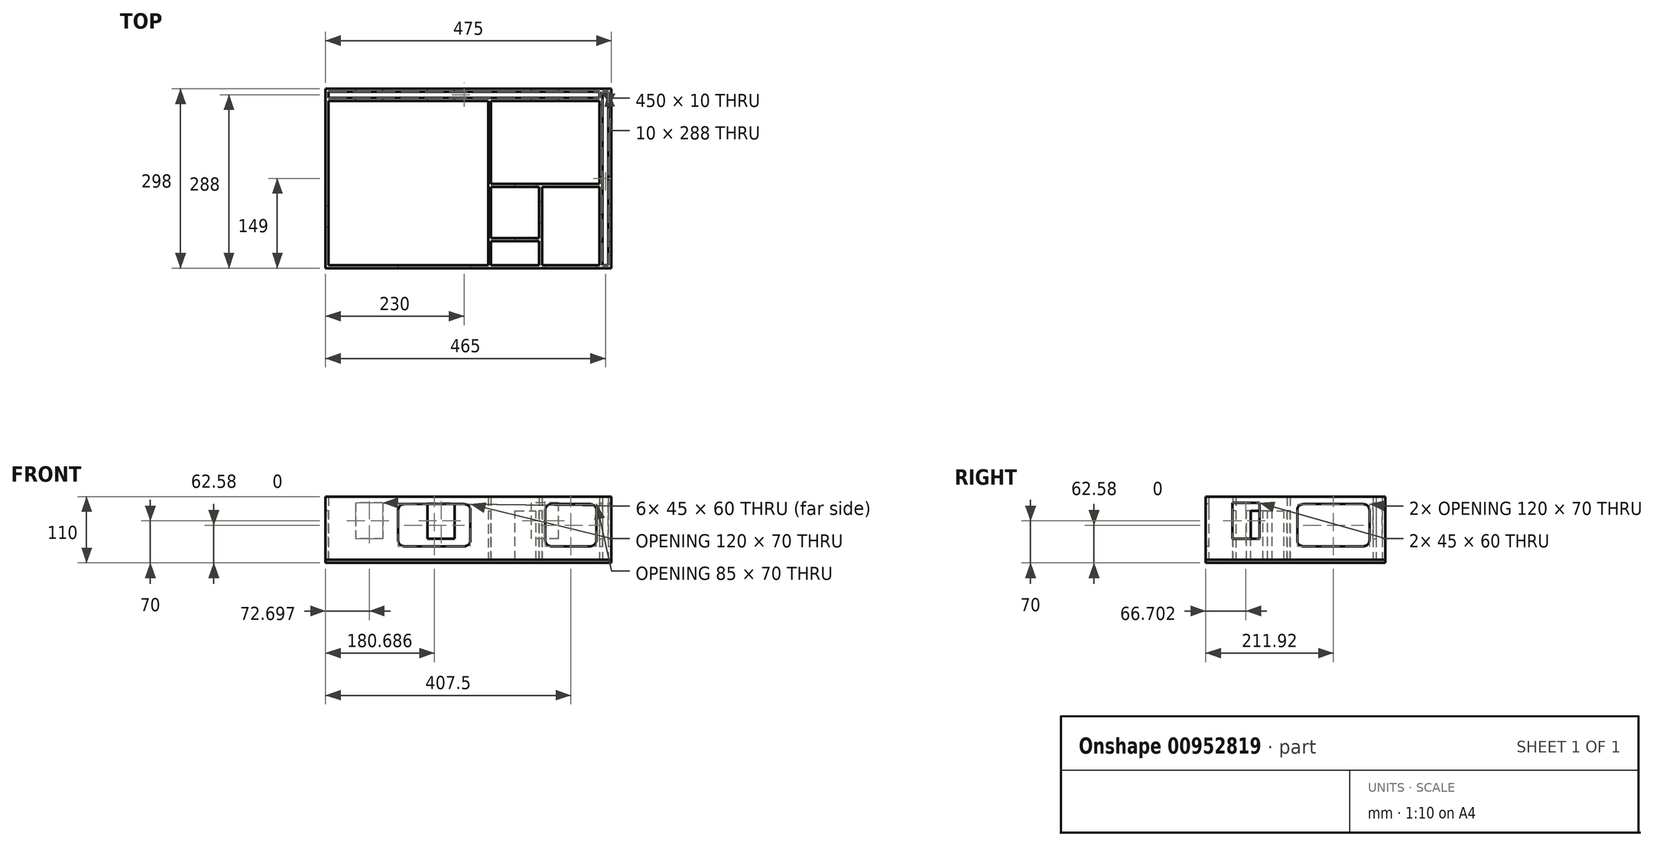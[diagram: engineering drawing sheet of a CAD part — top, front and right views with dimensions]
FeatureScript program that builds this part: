
annotation { "Feature Type Name" : "Feature", "Feature Type Description" : "" }
export const myFeature = defineFeature(function(context is Context, id is Id, definition is map)
    precondition{}
    {
        {
            var Q0;
            Q0=qCreatedBy(makeId("Top.planeOp"),FACE);
            var sketch = newSketch(context, id + "F0", { "sketchPlane" : qUnion([Q0])});
            skLineSegment(sketch, "E0.bottom", {"start": v(237.5, -149) * mm, "end": v(-237.5, -149) * mm});
            skLineSegment(sketch, "E0.top", {"start": v(237.5, 149) * mm, "end": v(-237.5, 149) * mm});
            skLineSegment(sketch, "E0.left", {"start": v(237.5, -149) * mm, "end": v(237.5, 149) * mm});
            skLineSegment(sketch, "E0.right", {"start": v(-237.5, -149) * mm, "end": v(-237.5, 149) * mm});
            skPoint(sketch, "E0.middle", {"position": v(0, 0) * mm});
            skSolve(sketch);
        }
        {
            var Q0;
            Q0 = qSketchRegion(id + "F0", true);
            extrude(context, id + "F1", {"entities" : qUnion([Q0]), "oppositeDirection" : true, "depth" : 5 * mm, "offsetDistance" : 25 * mm});
        }
        {
            var Q0;
            Q0=makeQuery(id+"F1.opExtrude","CAP_FACE",FACE,{"disambiguationData":[OSD([sQuery(id+"F0.wireOp",EDGE,"E0.bottom"),sQuery(id+"F0.wireOp",EDGE,"E0.top"),sQuery(id+"F0.wireOp",EDGE,"E0.left"),sQuery(id+"F0.wireOp",EDGE,"E0.right")])],"isStart":true});
            var sketch = newSketch(context, id + "F2", { "sketchPlane" : qUnion([Q0])});
            skLineSegment(sketch, "E1.0.0", {"start": v(237.5, -149) * mm, "end": v(237.5, 149) * mm});
            skLineSegment(sketch, "E1.0.1", {"start": v(237.5, 149) * mm, "end": v(-237.5, 149) * mm});
            skLineSegment(sketch, "E1.0.2", {"start": v(-237.5, 149) * mm, "end": v(-237.5, -149) * mm});
            skLineSegment(sketch, "E1.0.3", {"start": v(-237.5, -149) * mm, "end": v(237.5, -149) * mm});
            skLineSegment(sketch, "E2.0", {"start": v(232.5, -144) * mm, "end": v(232.5, 144) * mm});
            skLineSegment(sketch, "E2.1", {"start": v(-232.5, -144) * mm, "end": v(232.5, -144) * mm});
            skLineSegment(sketch, "E2.2", {"start": v(-232.5, 144) * mm, "end": v(-232.5, -144) * mm});
            skLineSegment(sketch, "E2.3", {"start": v(232.5, 144) * mm, "end": v(-232.5, 144) * mm});
            skLineSegment(sketch, "E3", {"start": v(-232.5, 134) * mm, "end": v(217.5, 134) * mm});
            skLineSegment(sketch, "E4", {"start": v(-232.5, 129) * mm, "end": v(217.5, 129) * mm});
            skLineSegment(sketch, "E5", {"start": v(32.5, 129) * mm, "end": v(32.5, -144) * mm});
            skLineSegment(sketch, "E6", {"start": v(37.5, -144) * mm, "end": v(37.5, 129) * mm});
            skLineSegment(sketch, "E7", {"start": v(222.5, 144) * mm, "end": v(222.5, -144) * mm});
            skLineSegment(sketch, "E8", {"start": v(217.5, 144) * mm, "end": v(217.5, -144) * mm});
            skLineSegment(sketch, "E9", {"start": v(117.5, -14) * mm, "end": v(117.5, -144) * mm});
            skLineSegment(sketch, "E10", {"start": v(122.5, -14) * mm, "end": v(122.5, -144) * mm});
            skLineSegment(sketch, "E11", {"start": v(37.5, -9) * mm, "end": v(217.5, -9) * mm});
            skLineSegment(sketch, "E12", {"start": v(37.5, -14) * mm, "end": v(217.5, -14) * mm});
            skLineSegment(sketch, "E13", {"start": v(117.5, -99) * mm, "end": v(37.5, -99) * mm});
            skLineSegment(sketch, "E14", {"start": v(117.5, -104) * mm, "end": v(37.5, -104) * mm});
            skLineSegment(sketch, "E15", {"start": v(73.5, -104) * mm, "end": v(73.5, -144) * mm, "construction": true});
            skSolve(sketch);
        }
        {
            var Q0;
            Q0=makeQuery(id+"F2.imprint","IMPRINT",FACE,{"disambiguationData":[TD([[makeQuery(id+"F2.imprint","IMPRINT",EDGE,{"derivedFrom":sQuery(id+"F2.wireOp",EDGE,"E1.0.0")}),1.0]])]});
            var Q1;
            {var subQ4=sQuery(id+"F2.wireOp",EDGE,"afQwtqYh-coUw-1QRY-l5fW-YoJflLdhl2Ut");Q1=makeQuery(id+"F2.imprint","IMPRINT",FACE,{"disambiguationData":[TD([[makeQuery(id+"F2.imprint","IMPRINT",EDGE,{"derivedFrom":subQ4}),1.0]])]});}
            var Q2;
            {var subQ5=sQuery(id+"F2.wireOp",EDGE,"E3");Q2=makeQuery(id+"F2.imprint","IMPRINT",FACE,{"disambiguationData":[TD([[makeQuery(id+"F2.imprint","IMPRINT",EDGE,{"derivedFrom":subQ5}),-1.0]])]});}
            var Q3;
            {var subQ0=sQuery(id+"F2.wireOp",EDGE,"E5");Q3=makeQuery(id+"F2.imprint","IMPRINT",FACE,{"disambiguationData":[TD([[makeQuery(id+"F2.imprint","IMPRINT",EDGE,{"derivedFrom":subQ0}),1.0]])]});}
            var Q4;
            {var subQ0=sQuery(id+"F2.wireOp",EDGE,"E7");Q4=makeQuery(id+"F2.imprint","IMPRINT",FACE,{"disambiguationData":[TD([[makeQuery(id+"F2.imprint","IMPRINT",EDGE,{"derivedFrom":subQ0}),-1.0]])]});}
            var Q5;
            {var subQ0=sQuery(id+"F2.wireOp",EDGE,"E9");Q5=makeQuery(id+"F2.imprint","IMPRINT",FACE,{"disambiguationData":[TD([[makeQuery(id+"F2.imprint","IMPRINT",EDGE,{"derivedFrom":subQ0}),1.0]])]});}
            var Q6;
            {var subQ0=sQuery(id+"F2.wireOp",EDGE,"E11");Q6=makeQuery(id+"F2.imprint","IMPRINT",FACE,{"disambiguationData":[TD([[makeQuery(id+"F2.imprint","IMPRINT",EDGE,{"derivedFrom":subQ0}),-1.0]])]});}
            var Q7;
            {var subQ0=sQuery(id+"F2.wireOp",EDGE,"E13");Q7=makeQuery(id+"F2.imprint","IMPRINT",FACE,{"disambiguationData":[TD([[makeQuery(id+"F2.imprint","IMPRINT",EDGE,{"derivedFrom":subQ0}),1.0]])]});}
            extrude(context, id + "F3", {"entities" : qUnion([Q0, Q1, Q2, Q3, Q4, Q5, Q6, Q7]), "depth" : 105 * mm, "offsetDistance" : 25 * mm});
        }
        {
            var Q0;
            Q0=makeQuery(id+"F3.boolean.opBoolean","MERGE",FACE,{"derivedFrom":[makeQuery(id+"F1.opExtrude","SWEPT_FACE",FACE,{"disambiguationData":[OSD([sQuery(id+"F0.wireOp",EDGE,"E0.top")])]}),makeQuery(id+"F3.opExtrude","SWEPT_FACE",FACE,{"disambiguationData":[OSD([sQuery(id+"F2.wireOp",EDGE,"E1.0.1")])]})]});
            var sketch = newSketch(context, id + "F4", { "sketchPlane" : qUnion([Q0])});
            skLineSegment(sketch, "E16.bottom", {"start": v(142.3, 95) * mm, "end": v(187.3, 95) * mm});
            skLineSegment(sketch, "E16.top", {"start": v(142.3, 35) * mm, "end": v(187.3, 35) * mm});
            skLineSegment(sketch, "E16.left", {"start": v(142.3, 95) * mm, "end": v(142.3, 35) * mm});
            skLineSegment(sketch, "E16.right", {"start": v(187.3, 95) * mm, "end": v(187.3, 35) * mm});
            skLineSegment(sketch, "E17.bottom", {"start": v(-104.37, 95) * mm, "end": v(-149.37, 95) * mm});
            skLineSegment(sketch, "E17.top", {"start": v(-104.37, 35) * mm, "end": v(-149.37, 35) * mm});
            skLineSegment(sketch, "E17.left", {"start": v(-104.37, 95) * mm, "end": v(-104.37, 35) * mm});
            skLineSegment(sketch, "E17.right", {"start": v(-149.37, 95) * mm, "end": v(-149.37, 35) * mm});
            skLineSegment(sketch, "E18.bottom", {"start": v(68.09, 95) * mm, "end": v(23.09, 95) * mm});
            skLineSegment(sketch, "E18.top", {"start": v(68.09, 35) * mm, "end": v(23.09, 35) * mm});
            skLineSegment(sketch, "E18.left", {"start": v(68.09, 95) * mm, "end": v(68.09, 35) * mm});
            skLineSegment(sketch, "E18.right", {"start": v(23.09, 95) * mm, "end": v(23.09, 35) * mm});
            skSolve(sketch);
        }
        {
            var Q0;
            Q0=makeQuery(id+"F4.imprint","IMPRINT",FACE,{"disambiguationData":[TD([[makeQuery(id+"F4.imprint","IMPRINT",EDGE,{"derivedFrom":sQuery(id+"F4.wireOp",EDGE,"E16.bottom")}),-1.0]])]});
            var Q1;
            Q1=makeQuery(id+"F4.imprint","IMPRINT",FACE,{"disambiguationData":[TD([[makeQuery(id+"F4.imprint","IMPRINT",EDGE,{"derivedFrom":sQuery(id+"F4.wireOp",EDGE,"RJ00ArhV-Cqba-DMyC-vLh9-4VJwI8xNZmvk.bottom")}),1.0]])]});
            var Q2;
            Q2=makeQuery(id+"F4.imprint","IMPRINT",FACE,{"disambiguationData":[TD([[makeQuery(id+"F4.imprint","IMPRINT",EDGE,{"derivedFrom":sQuery(id+"F4.wireOp",EDGE,"E17.bottom")}),1.0]])]});
            var Q3;
            Q3=makeQuery(id+"F4.imprint","IMPRINT",FACE,{"disambiguationData":[TD([[makeQuery(id+"F4.imprint","IMPRINT",EDGE,{"derivedFrom":sQuery(id+"F4.wireOp",EDGE,"E18.bottom")}),1.0]])]});
            var Q4;
            {var subQ0=sQuery(id+"F2.wireOp",EDGE,"E4");Q4=makeQuery(id+"F3.opExtrude","SWEPT_FACE",FACE,{"disambiguationData":[OSD([subQ0]),TDD([makeQuery(id+"F2.imprint","IMPRINT",EDGE,{"disambiguationData":[TD([[makeQuery(id+"F2.imprint","INTERSECT",VERTEX,{"derivedFrom":[sQuery(id+"F2.wireOp",EDGE,"auQAcFBx-aoKs-4rH1-USsh-kt6OsAu8T3Fz"),subQ0]}),-1.0]])],"derivedFrom":subQ0})])]});}
            extrude(context, id + "F5", {"entities" : qUnion([Q0, Q1, Q2, Q3]), "operationType" : NewBodyOperationType.REMOVE, "endBound" : BoundingType.UP_TO_SURFACE, "oppositeDirection" : true, "depth" : 25 * mm, "endBoundEntityFace" : qUnion([Q4]), "offsetDistance" : 25 * mm});
        }
        {
            var Q0;
            Q0=makeQuery(id+"F3.boolean.opBoolean","MERGE",FACE,{"derivedFrom":[makeQuery(id+"F1.opExtrude","SWEPT_FACE",FACE,{"disambiguationData":[OSD([sQuery(id+"F0.wireOp",EDGE,"E0.bottom")])]}),makeQuery(id+"F3.opExtrude","SWEPT_FACE",FACE,{"disambiguationData":[OSD([sQuery(id+"F2.wireOp",EDGE,"E1.0.3")])]})]});
            var sketch = newSketch(context, id + "F6", { "sketchPlane" : qUnion([Q0])});
            skLineSegment(sketch, "E19.left", {"start": v(-186.1, 0) * mm, "end": v(-186.1, 0) * mm});
            skLineSegment(sketch, "E20.bottom", {"start": v(-6.81, 92.58) * mm, "end": v(-106.81, 92.58) * mm});
            skLineSegment(sketch, "E20.top", {"start": v(-6.81, 22.58) * mm, "end": v(-106.81, 22.58) * mm});
            skLineSegment(sketch, "E20.left", {"start": v(3.19, 82.58) * mm, "end": v(3.19, 32.58) * mm});
            skLineSegment(sketch, "E20.right", {"start": v(-116.81, 82.58) * mm, "end": v(-116.81, 32.58) * mm});
            skPoint(sketch, "E21.visualSharp", {"position": v(-116.81, 92.58) * mm});
            skArc(sketch, "E21.filletArc", {"start": v(-106.81, 92.58) * mm, "mid": v(-113.88, 89.65) * mm, "end": v(-116.81, 82.58) * mm});
            skPoint(sketch, "E22.visualSharp", {"position": v(3.19, 92.58) * mm});
            skArc(sketch, "E22.filletArc", {"start": v(3.19, 82.58) * mm, "mid": v(0.26, 89.65) * mm, "end": v(-6.81, 92.58) * mm});
            skPoint(sketch, "E23.visualSharp", {"position": v(3.19, 22.58) * mm});
            skArc(sketch, "E23.filletArc", {"start": v(-6.81, 22.58) * mm, "mid": v(0.26, 25.5) * mm, "end": v(3.19, 32.58) * mm});
            skPoint(sketch, "E24.visualSharp", {"position": v(-116.81, 22.58) * mm});
            skArc(sketch, "E24.filletArc", {"start": v(-116.81, 32.58) * mm, "mid": v(-113.88, 25.5) * mm, "end": v(-106.81, 22.58) * mm});
            skLineSegment(sketch, "E25.bottom", {"start": v(137.5, 92.58) * mm, "end": v(202.5, 92.58) * mm});
            skLineSegment(sketch, "E25.top", {"start": v(137.5, 22.58) * mm, "end": v(202.5, 22.58) * mm});
            skLineSegment(sketch, "E25.left", {"start": v(127.5, 82.58) * mm, "end": v(127.5, 32.58) * mm});
            skLineSegment(sketch, "E25.right", {"start": v(212.5, 82.58) * mm, "end": v(212.5, 32.58) * mm});
            skPoint(sketch, "E26.visualSharp", {"position": v(127.5, 92.58) * mm});
            skArc(sketch, "E26.filletArc", {"start": v(137.5, 92.58) * mm, "mid": v(130.43, 89.65) * mm, "end": v(127.5, 82.58) * mm});
            skPoint(sketch, "E27.visualSharp", {"position": v(212.5, 92.58) * mm});
            skArc(sketch, "E27.filletArc", {"start": v(212.5, 82.58) * mm, "mid": v(209.57, 89.65) * mm, "end": v(202.5, 92.58) * mm});
            skPoint(sketch, "E28.visualSharp", {"position": v(212.5, 22.58) * mm});
            skArc(sketch, "E28.filletArc", {"start": v(202.5, 22.58) * mm, "mid": v(209.57, 25.5) * mm, "end": v(212.5, 32.58) * mm});
            skPoint(sketch, "E29.visualSharp", {"position": v(127.5, 22.58) * mm});
            skArc(sketch, "E29.filletArc", {"start": v(127.5, 32.58) * mm, "mid": v(130.43, 25.5) * mm, "end": v(137.5, 22.58) * mm});
            skLineSegment(sketch, "E30.0.1", {"start": v(37.5, 0) * mm, "end": v(37.5, 105) * mm, "construction": true});
            skLineSegment(sketch, "E30.0.2", {"start": v(37.5, 105) * mm, "end": v(117.5, 105) * mm, "construction": true});
            skLineSegment(sketch, "E30.0.3", {"start": v(117.5, 105) * mm, "end": v(117.5, 0) * mm, "construction": true});
            skSolve(sketch);
        }
        {
            var Q0;
            Q0=makeQuery(id+"F6.imprint","IMPRINT",FACE,{"disambiguationData":[TD([[makeQuery(id+"F6.imprint","IMPRINT",EDGE,{"derivedFrom":sQuery(id+"F6.wireOp",EDGE,"E19.bottom")}),-1.0]])]});
            var Q1;
            Q1=makeQuery(id+"F6.imprint","IMPRINT",FACE,{"disambiguationData":[TD([[makeQuery(id+"F6.imprint","IMPRINT",EDGE,{"derivedFrom":sQuery(id+"F6.wireOp",EDGE,"E20.bottom")}),1.0]])]});
            var Q2;
            Q2=makeQuery(id+"F6.imprint","IMPRINT",FACE,{"disambiguationData":[TD([[makeQuery(id+"F6.imprint","IMPRINT",EDGE,{"derivedFrom":sQuery(id+"F6.wireOp",EDGE,"E25.bottom")}),-1.0]])]});
            var Q3;
            {var subQ0=sQuery(id+"F2.wireOp",EDGE,"E2.1");Q3=makeQuery(id+"F3.opExtrude","SWEPT_FACE",FACE,{"disambiguationData":[OSD([subQ0]),TDD([makeQuery(id+"F2.imprint","IMPRINT",EDGE,{"disambiguationData":[TD([[makeQuery(id+"F2.imprint","INTERSECT",VERTEX,{"derivedFrom":[subQ0,sQuery(id+"F2.wireOp",EDGE,"E2.2")]}),-1.0]])],"derivedFrom":subQ0})])]});}
            extrude(context, id + "F7", {"entities" : qUnion([Q0, Q1, Q2]), "operationType" : NewBodyOperationType.REMOVE, "endBound" : BoundingType.UP_TO_SURFACE, "oppositeDirection" : true, "depth" : 25 * mm, "endBoundEntityFace" : qUnion([Q3]), "offsetDistance" : 25 * mm});
        }
        {
            var Q0;
            Q0=makeQuery(id+"F3.opExtrude","SWEPT_FACE",FACE,{"disambiguationData":[OSD([sQuery(id+"F2.wireOp",EDGE,"E1.0.0")])]});
            var sketch = newSketch(context, id + "F8", { "sketchPlane" : qUnion([Q0])});
            skLineSegment(sketch, "E31.bottom", {"start": v(-104.8, 95) * mm, "end": v(-59.8, 95) * mm});
            skLineSegment(sketch, "E31.top", {"start": v(-104.8, 35) * mm, "end": v(-59.8, 35) * mm});
            skLineSegment(sketch, "E31.left", {"start": v(-104.8, 95) * mm, "end": v(-104.8, 35) * mm});
            skLineSegment(sketch, "E31.right", {"start": v(-59.8, 95) * mm, "end": v(-59.8, 35) * mm});
            skLineSegment(sketch, "E32.bottom", {"start": v(12.92, 92.58) * mm, "end": v(112.92, 92.58) * mm});
            skLineSegment(sketch, "E32.top", {"start": v(12.92, 22.58) * mm, "end": v(112.92, 22.58) * mm});
            skLineSegment(sketch, "E32.left", {"start": v(2.92, 82.58) * mm, "end": v(2.92, 32.58) * mm});
            skLineSegment(sketch, "E32.right", {"start": v(122.92, 82.58) * mm, "end": v(122.92, 32.58) * mm});
            skPoint(sketch, "E33.visualSharp", {"position": v(2.92, 92.58) * mm});
            skArc(sketch, "E33.filletArc", {"start": v(12.92, 92.58) * mm, "mid": v(5.85, 89.65) * mm, "end": v(2.92, 82.58) * mm});
            skPoint(sketch, "E34.visualSharp", {"position": v(122.92, 92.58) * mm});
            skArc(sketch, "E34.filletArc", {"start": v(122.92, 82.58) * mm, "mid": v(120, 89.65) * mm, "end": v(112.92, 92.58) * mm});
            skPoint(sketch, "E35.visualSharp", {"position": v(122.92, 22.58) * mm});
            skArc(sketch, "E35.filletArc", {"start": v(112.92, 22.58) * mm, "mid": v(120, 25.5) * mm, "end": v(122.92, 32.58) * mm});
            skPoint(sketch, "E36.visualSharp", {"position": v(2.92, 22.58) * mm});
            skArc(sketch, "E36.filletArc", {"start": v(2.92, 32.58) * mm, "mid": v(5.85, 25.5) * mm, "end": v(12.92, 22.58) * mm});
            skSolve(sketch);
        }
        {
            var Q0;
            Q0=makeQuery(id+"F8.imprint","IMPRINT",FACE,{"disambiguationData":[TD([[makeQuery(id+"F8.imprint","IMPRINT",EDGE,{"derivedFrom":sQuery(id+"F8.wireOp",EDGE,"E31.bottom")}),-1.0]])]});
            var Q1;
            Q1=makeQuery(id+"F8.imprint","IMPRINT",FACE,{"disambiguationData":[TD([[makeQuery(id+"F8.imprint","IMPRINT",EDGE,{"derivedFrom":sQuery(id+"F8.wireOp",EDGE,"E32.bottom")}),-1.0]])]});
            var Q2;
            {var subQ0=sQuery(id+"F2.wireOp",EDGE,"E8");Q2=makeQuery(id+"F3.opExtrude","SWEPT_FACE",FACE,{"disambiguationData":[OSD([subQ0]),TDD([makeQuery(id+"F2.imprint","IMPRINT",EDGE,{"disambiguationData":[TD([[makeQuery(id+"F2.imprint","INTERSECT",VERTEX,{"derivedFrom":[sQuery(id+"F2.wireOp",EDGE,"E4"),subQ0]}),-1.0]])],"derivedFrom":subQ0})])]});}
            extrude(context, id + "F9", {"entities" : qUnion([Q0, Q1]), "operationType" : NewBodyOperationType.REMOVE, "endBound" : BoundingType.UP_TO_SURFACE, "oppositeDirection" : true, "depth" : 25 * mm, "endBoundEntityFace" : qUnion([Q2]), "offsetDistance" : 25 * mm});
        }
        {
            var Q0;
            Q0=makeQuery(id+"F3.opExtrude","SWEPT_FACE",FACE,{"disambiguationData":[OSD([sQuery(id+"F2.wireOp",EDGE,"E6")])]});
            var sketch = newSketch(context, id + "F10", { "sketchPlane" : qUnion([Q0])});
            skLineSegment(sketch, "E37.bottom", {"start": v(-54, 0) * mm, "end": v(-19, 0) * mm});
            skLineSegment(sketch, "E37.top", {"start": v(-54, 81.6) * mm, "end": v(-19, 81.6) * mm});
            skLineSegment(sketch, "E37.left", {"start": v(-54, 0) * mm, "end": v(-54, 81.6) * mm});
            skLineSegment(sketch, "E37.right", {"start": v(-19, 0) * mm, "end": v(-19, 81.6) * mm});
            skSolve(sketch);
        }
        {
            var Q0;
            Q0=makeQuery(id+"F10.imprint","IMPRINT",FACE,{"disambiguationData":[TD([[makeQuery(id+"F10.imprint","IMPRINT",EDGE,{"derivedFrom":sQuery(id+"F10.wireOp",EDGE,"E37.bottom")}),1.0]])]});
            extrude(context, id + "F11", {"entities" : qUnion([Q0]), "operationType" : NewBodyOperationType.REMOVE, "endBound" : BoundingType.UP_TO_NEXT, "oppositeDirection" : true, "depth" : 25 * mm, "offsetDistance" : 25 * mm});
        }
        {
            var Q0;
            Q0=makeQuery(id+"F3.opExtrude","SWEPT_FACE",FACE,{"disambiguationData":[OSD([sQuery(id+"F2.wireOp",EDGE,"E9")])]});
            var sketch = newSketch(context, id + "F12", { "sketchPlane" : qUnion([Q0])});
            skLineSegment(sketch, "E38.bottom", {"start": v(39, 0) * mm, "end": v(74, 0) * mm});
            skLineSegment(sketch, "E38.top", {"start": v(39, 81.6) * mm, "end": v(74, 81.6) * mm});
            skLineSegment(sketch, "E38.left", {"start": v(39, 0) * mm, "end": v(39, 81.6) * mm});
            skLineSegment(sketch, "E38.right", {"start": v(74, 0) * mm, "end": v(74, 81.6) * mm});
            skLineSegment(sketch, "E39.0", {"start": v(14, 105) * mm, "end": v(14, 0) * mm});
            skPoint(sketch, "E40", {"position": v(56.5, 0) * mm});
            skSolve(sketch);
        }
        {
            var Q0;
            Q0=makeQuery(id+"F12.imprint","IMPRINT",FACE,{"disambiguationData":[TD([[makeQuery(id+"F12.imprint","IMPRINT",EDGE,{"derivedFrom":sQuery(id+"F12.wireOp",EDGE,"RfPehwQf-eHDW-nS7q-FXhD-8PPsaDqkBPPb.bottom")}),1.0]])]});
            var Q1;
            Q1=makeQuery(id+"F12.imprint","IMPRINT",FACE,{"disambiguationData":[TD([[makeQuery(id+"F12.imprint","IMPRINT",EDGE,{"derivedFrom":sQuery(id+"F12.wireOp",EDGE,"E38.bottom")}),1.0]])]});
            extrude(context, id + "F13", {"entities" : qUnion([Q0, Q1]), "operationType" : NewBodyOperationType.REMOVE, "endBound" : BoundingType.UP_TO_NEXT, "oppositeDirection" : true, "depth" : 25 * mm, "offsetDistance" : 25 * mm});
        }
        {
            var Q0;
            Q0=makeQuery(id+"F3.opExtrude","SWEPT_FACE",FACE,{"disambiguationData":[OSD([sQuery(id+"F2.wireOp",EDGE,"E14")])]});
            var sketch = newSketch(context, id + "F14", { "sketchPlane" : qUnion([Q0])});
            skLineSegment(sketch, "E41.bottom", {"start": v(77.5, 0) * mm, "end": v(112.5, 0) * mm});
            skLineSegment(sketch, "E41.top", {"start": v(77.5, 81.6) * mm, "end": v(112.5, 81.6) * mm});
            skLineSegment(sketch, "E41.left", {"start": v(77.5, 0) * mm, "end": v(77.5, 81.6) * mm});
            skLineSegment(sketch, "E41.right", {"start": v(112.5, 0) * mm, "end": v(112.5, 81.6) * mm});
            skLineSegment(sketch, "E42", {"start": v(112.5, 0) * mm, "end": v(77.5, 0) * mm});
            skSolve(sketch);
        }
        {
            var Q0;
            Q0=makeQuery(id+"F14.imprint","IMPRINT",FACE,{"disambiguationData":[TD([[makeQuery(id+"F14.imprint","IMPRINT",EDGE,{"derivedFrom":sQuery(id+"F14.wireOp",EDGE,"E41.top")}),-1.0]])]});
            extrude(context, id + "F15", {"entities" : qUnion([Q0]), "operationType" : NewBodyOperationType.REMOVE, "endBound" : BoundingType.UP_TO_NEXT, "oppositeDirection" : true, "depth" : 25 * mm, "offsetDistance" : 25 * mm});
        }
        {
            var Q0;
            {var subQ0=sQuery(id+"F2.wireOp",EDGE,"E12");Q0=makeQuery(id+"F3.opExtrude","SWEPT_FACE",FACE,{"disambiguationData":[OSD([subQ0]),TDD([makeQuery(id+"F2.imprint","IMPRINT",EDGE,{"disambiguationData":[TD([[makeQuery(id+"F2.imprint","INTERSECT",VERTEX,{"derivedFrom":[sQuery(id+"F2.wireOp",EDGE,"E9"),subQ0]}),1.0]])],"derivedFrom":subQ0})])]});}
            var sketch = newSketch(context, id + "F16", { "sketchPlane" : qUnion([Q0])});
            skLineSegment(sketch, "E43.bottom", {"start": v(77.5, 0) * mm, "end": v(112.5, 0) * mm});
            skLineSegment(sketch, "E43.top", {"start": v(77.5, 81.6) * mm, "end": v(112.5, 81.6) * mm});
            skLineSegment(sketch, "E43.left", {"start": v(77.5, 0) * mm, "end": v(77.5, 81.6) * mm});
            skLineSegment(sketch, "E43.right", {"start": v(112.5, 0) * mm, "end": v(112.5, 81.6) * mm});
            skSolve(sketch);
        }
        {
            var Q0;
            Q0=makeQuery(id+"F16.imprint","IMPRINT",FACE,{"disambiguationData":[TD([[makeQuery(id+"F16.imprint","IMPRINT",EDGE,{"derivedFrom":sQuery(id+"F16.wireOp",EDGE,"E43.bottom")}),1.0]])]});
            extrude(context, id + "F17", {"entities" : qUnion([Q0]), "operationType" : NewBodyOperationType.REMOVE, "endBound" : BoundingType.UP_TO_NEXT, "oppositeDirection" : true, "depth" : 25 * mm, "offsetDistance" : 25 * mm});
        }
        {
            var Q0;
            Q0=makeQuery(id+"F3.opExtrude","SWEPT_FACE",FACE,{"disambiguationData":[OSD([sQuery(id+"F2.wireOp",EDGE,"E1.0.2")])]});
            var sketch = newSketch(context, id + "F18", { "sketchPlane" : qUnion([Q0])});
            skLineSegment(sketch, "E44.bottom", {"start": v(46.14, 0) * mm, "end": v(81.14, 0) * mm});
            skLineSegment(sketch, "E44.top", {"start": v(46.14, 81.6) * mm, "end": v(81.14, 81.6) * mm});
            skLineSegment(sketch, "E44.left", {"start": v(46.14, 0) * mm, "end": v(46.14, 81.6) * mm});
            skLineSegment(sketch, "E44.right", {"start": v(81.14, 0) * mm, "end": v(81.14, 81.6) * mm});
            skSolve(sketch);
        }
        {
            var Q0;
            Q0=makeQuery(id+"F18.imprint","IMPRINT",FACE,{"disambiguationData":[TD([[makeQuery(id+"F18.imprint","IMPRINT",EDGE,{"derivedFrom":sQuery(id+"F18.wireOp",EDGE,"E44.bottom")}),-1.0]])]});
            extrude(context, id + "F19", {"entities" : qUnion([Q0]), "operationType" : NewBodyOperationType.REMOVE, "endBound" : BoundingType.UP_TO_NEXT, "oppositeDirection" : true, "depth" : 25 * mm, "offsetDistance" : 25 * mm});
        }
    });
